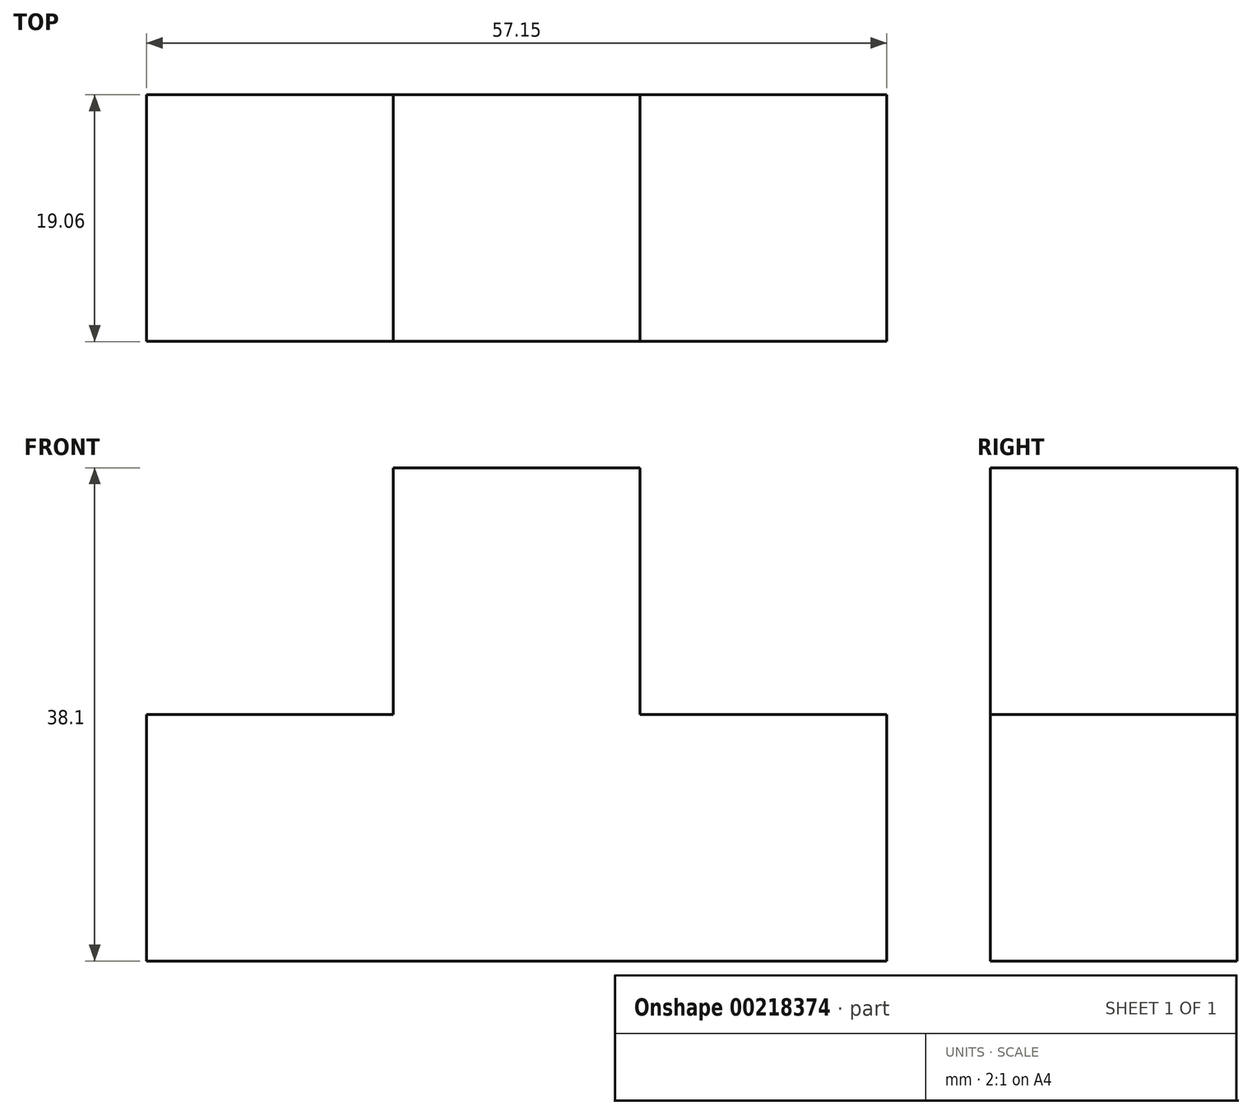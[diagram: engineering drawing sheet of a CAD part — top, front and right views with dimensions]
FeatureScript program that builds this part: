
annotation { "Feature Type Name" : "Feature", "Feature Type Description" : "" }
export const myFeature = defineFeature(function(context is Context, id is Id, definition is map)
    precondition{}
    {
        {
            var Q0;
            Q0=qCreatedBy(makeId("Front.planeOp"),FACE);
            var sketch = newSketch(context, id + "F0", { "sketchPlane" : qUnion([Q0])});
            skLineSegment(sketch, "E0", {"start": v(-46.04, -35.4) * mm, "end": v(11.1, -35.4) * mm});
            skLineSegment(sketch, "E1", {"start": v(11.1, -16.36) * mm, "end": v(-7.94, -16.36) * mm});
            skLineSegment(sketch, "E2", {"start": v(-7.94, -16.36) * mm, "end": v(-7.94, 2.7) * mm});
            skLineSegment(sketch, "E3", {"start": v(-7.94, 2.7) * mm, "end": v(-27, 2.7) * mm});
            skLineSegment(sketch, "E4", {"start": v(-27, 2.7) * mm, "end": v(-27, -16.36) * mm});
            skLineSegment(sketch, "E5", {"start": v(-27, -16.36) * mm, "end": v(-46.04, -16.36) * mm});
            skLineSegment(sketch, "E6", {"start": v(-46.04, -16.36) * mm, "end": v(-46.04, -35.4) * mm});
            skLineSegment(sketch, "E7", {"start": v(11.1, -35.4) * mm, "end": v(11.1, -16.36) * mm});
            skSolve(sketch);
        }
        {
            var Q0;
            Q0 = qSketchRegion(id + "F0", true);
            extrude(context, id + "F1", {"entities" : qUnion([Q0]), "endBound" : BoundingType.SYMMETRIC, "depth" : 19.05 * mm});
        }
        {
            var Q0;
            Q0 = qSketchRegion(id + "F0", true);
            extrude(context, id + "F2", {"entities" : qUnion([Q0]), "operationType" : NewBodyOperationType.ADD, "endBound" : BoundingType.SYMMETRIC, "depth" : 19.05 * mm});
        }
    });
